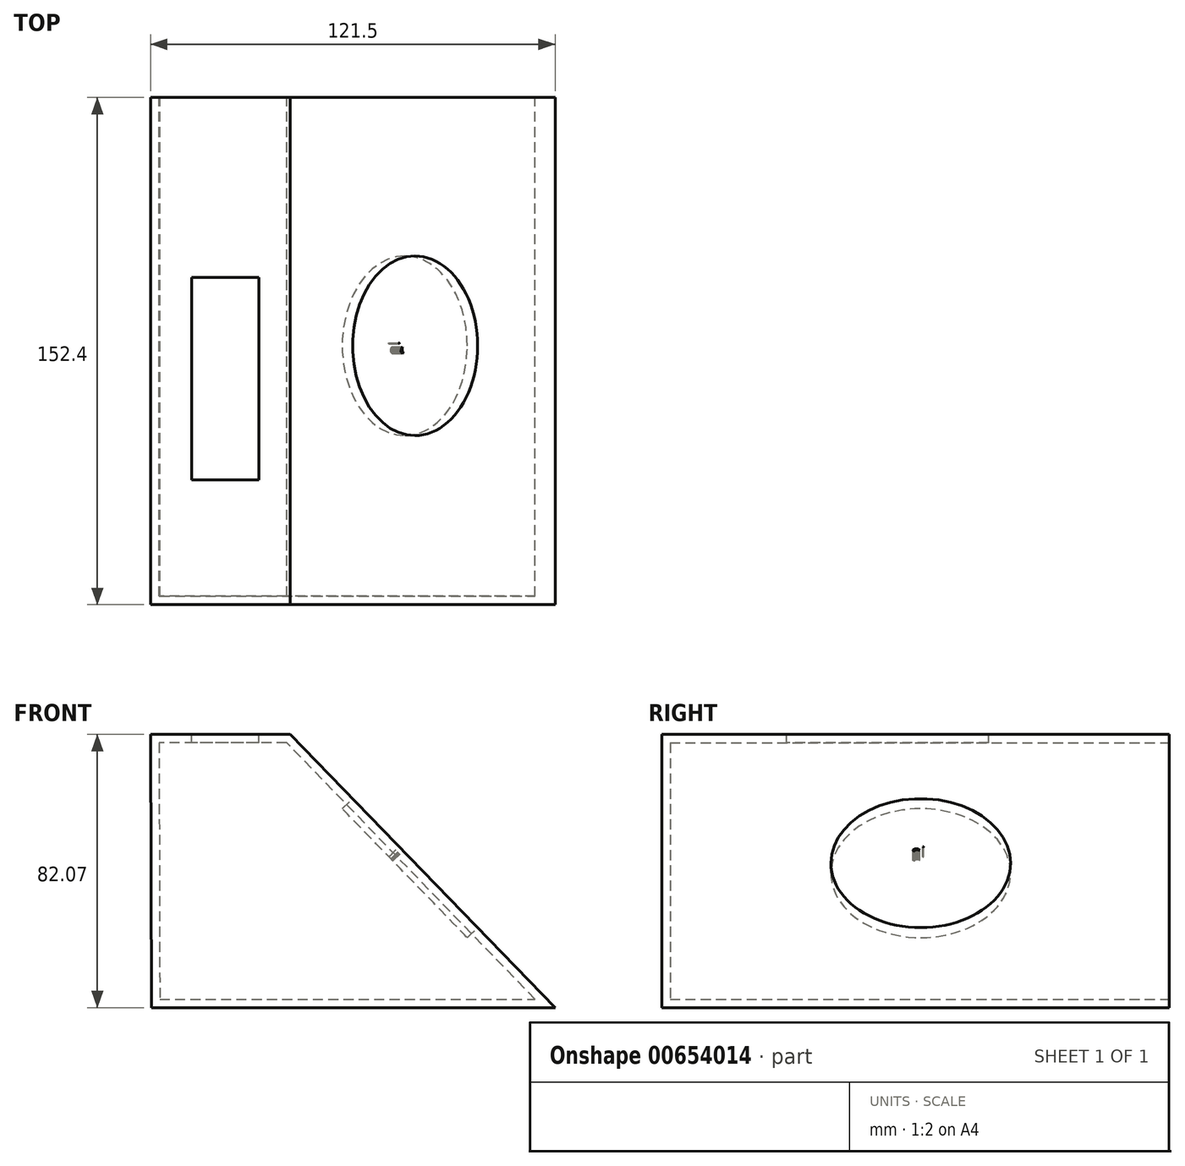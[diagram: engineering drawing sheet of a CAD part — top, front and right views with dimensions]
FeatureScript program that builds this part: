
annotation { "Feature Type Name" : "Feature", "Feature Type Description" : "" }
export const myFeature = defineFeature(function(context is Context, id is Id, definition is map)
    precondition{}
    {
        {
            var Q0;
            Q0=qCreatedBy(makeId("Front.planeOp"),FACE);
            var sketch = newSketch(context, id + "F0", { "sketchPlane" : qUnion([Q0])});
            skLineSegment(sketch, "E0", {"start": v(-59.5, -35.42) * mm, "end": v(61.78, -35.42) * mm});
            skLineSegment(sketch, "E1", {"start": v(61.78, -35.42) * mm, "end": v(-17.77, 46.65) * mm});
            skLineSegment(sketch, "E2", {"start": v(-17.77, 46.65) * mm, "end": v(-59.72, 46.65) * mm});
            skLineSegment(sketch, "E3", {"start": v(-59.72, 46.65) * mm, "end": v(-59.5, -35.42) * mm});
            skSolve(sketch);
        }
        {
            var Q0;
            Q0=makeQuery(id+"F0.imprint","IMPRINT",FACE,{"disambiguationData":[TD([[makeQuery(id+"F0.imprint","IMPRINT",EDGE,{"derivedFrom":sQuery(id+"F0.wireOp",EDGE,"E0")}),1.0]])]});
            extrude(context, id + "F1", {"entities" : qUnion([Q0]), "depth" : 152.4 * mm, "offsetDistance" : 25.4 * mm});
        }
        {
            var Q0;
            Q0=makeQuery(id+"F1.opExtrude","CAP_FACE",FACE,{"disambiguationData":[OSD([sQuery(id+"F0.wireOp",EDGE,"E0"),sQuery(id+"F0.wireOp",EDGE,"E1"),sQuery(id+"F0.wireOp",EDGE,"E2"),sQuery(id+"F0.wireOp",EDGE,"E3")])],"isStart":true});
            var Q1;
            Q1=makeQuery(id+"FHftFUIEuzboTOy_1.boolean.opBoolean","COPY",FACE,{"derivedFrom":makeQuery(id+"FHftFUIEuzboTOy_1.opExtrude","SWEPT_FACE",FACE,{"disambiguationData":[OSD([sQuery(id+"FhygIm2fGgisZin_1.wireOp",EDGE,"3zrmq9q6-JKVG-zBgU-pCQW-6CpuXbiN4dUc.right")])]})});
            shell(context, id + "F2", {"entities" : qUnion([Q0, Q1]), "thickness" : 2.54 * mm});
        }
        {
            var Q0;
            Q0=makeQuery(id+"F1.opExtrude","SWEPT_FACE",FACE,{"disambiguationData":[OSD([sQuery(id+"F0.wireOp",EDGE,"E1")])]});
            var sketch = newSketch(context, id + "F3", { "sketchPlane" : qUnion([Q0])});
            skCircle(sketch, "E4", {"center": v(-74.6, -7.98) * mm, "radius": 26.98 * mm});
            skFitSpline(sketch, "E5", {"points": [v(-77.65, -4.2) * mm, v(-77.2, -4.2) * mm, v(-77.04, -3.74) * mm, v(-77.04, -3.39) * mm, v(-77.22, -3.21) * mm, v(-77.33, -3.02) * mm, v(-77.17, -2.94) * mm, v(-77.3, -2.87) * mm, v(-77.46, -2.87) * mm, v(-77.58, -2.67) * mm, v(-77.53, -2.42) * mm, v(-77.33, -2.4) * mm, v(-77.43, -2.23) * mm, v(-77.4, -2) * mm, v(-77.27, -1.84) * mm, v(-77.27, -1.53) * mm, v(-77.22, -1.3) * mm, v(-77.1, -1.24) * mm, v(-76.92, -1.24) * mm, v(-76.86, -1.15) * mm, v(-76.9, -0.95) * mm, v(-76.72, -0.86) * mm, v(-76.52, -0.86) * mm, v(-76.36, -0.97) * mm, v(-76.28, -1.07) * mm, v(-76.21, -1.26) * mm, v(-76.04, -1.24) * mm, v(-75.8, -1.38) * mm, v(-75.65, -1.53) * mm], "startDerivative": vector(10.08, -2.27) * mm, "endDerivative": vector(3.46, -4.3) * mm});
            skFitSpline(sketch, "E6", {"points": [v(-75.56, -1.51) * mm, v(-75.4, -1.63) * mm, v(-75.17, -1.74) * mm, v(-75.04, -1.9) * mm, v(-74.9, -1.98) * mm, v(-74.75, -2.15) * mm, v(-74.66, -2.34) * mm, v(-74.54, -2.38) * mm, v(-74.49, -2.5) * mm, v(-74.45, -2.17) * mm, v(-74.45, -1.94) * mm, v(-74.45, -1.8) * mm, v(-74.4, -1.96) * mm, v(-74.36, -1.65) * mm, v(-74.34, -1.78) * mm, v(-74.3, -1.44) * mm, v(-74.24, -1.59) * mm, v(-74.17, -1.3) * mm, v(-74.04, -1.2) * mm, v(-74.06, -1.36) * mm, v(-73.96, -1.07) * mm, v(-73.96, -1.2) * mm], "startDerivative": vector(3.2, -2.61) * mm, "endDerivative": vector(-0.57, -6) * mm});
            skFitSpline(sketch, "E7", {"points": [v(-77.65, -4.2) * mm, v(-77.65, -4.43) * mm, v(-77.48, -4.49) * mm, v(-77.33, -4.53) * mm, v(-77.2, -4.49) * mm, v(-77.07, -4.5) * mm, v(-76.9, -4.43) * mm, v(-76.77, -4.41) * mm, v(-76.72, -4.24) * mm, v(-76.63, -4.24) * mm, v(-76.61, -3.97) * mm, v(-76.54, -3.9) * mm, v(-76.46, -4.24) * mm, v(-76.32, -4.24) * mm, v(-76.24, -4.4) * mm, v(-76.06, -4.24) * mm, v(-75.9, -4.24) * mm, v(-75.72, -4.4) * mm, v(-75.53, -4.43) * mm, v(-75.47, -4.76) * mm, v(-75.32, -4.86) * mm, v(-75.2, -5.01) * mm, v(-75.25, -5.1) * mm, v(-75.24, -5.5) * mm, v(-75.06, -5.53) * mm, v(-75.02, -5.67) * mm, v(-74.9, -5.79) * mm, v(-74.92, -6) * mm, v(-75.11, -6.04) * mm, v(-75.25, -6.08) * mm, v(-75.3, -6.2) * mm, v(-75.21, -6.4) * mm, v(-75.03, -6.44) * mm, v(-74.88, -6.44) * mm, v(-74.74, -6.4) * mm, v(-74.54, -6.29) * mm, v(-74.42, -6.11) * mm, v(-74.3, -6.04) * mm, v(-74.18, -5.82) * mm, v(-74.07, -5.6) * mm, v(-73.95, -5.2) * mm, v(-73.95, -5.05) * mm, v(-73.95, -4.86) * mm, v(-73.95, -4.59) * mm, v(-73.95, -4.2) * mm, v(-73.95, -3.99) * mm, v(-73.95, -3.8) * mm, v(-73.95, -3.64) * mm, v(-73.71, -3.5) * mm, v(-73.54, -3.39) * mm, v(-73.35, -3.33) * mm, v(-73.18, -3.25) * mm, v(-73.06, -3.21) * mm, v(-73.02, -3.08) * mm, v(-73.03, -2.94) * mm, v(-73.13, -2.87) * mm, v(-73.27, -2.73) * mm, v(-73.43, -2.71) * mm, v(-73.67, -2.73) * mm, v(-73.8, -2.85) * mm, v(-73.95, -2.92) * mm, v(-73.95, -2.73) * mm, v(-73.95, -2.52) * mm, v(-73.95, -2.29) * mm, v(-73.95, -2.05) * mm, v(-73.78, -1.92) * mm, v(-73.64, -1.8) * mm, v(-73.43, -1.65) * mm, v(-73.25, -1.65) * mm, v(-73.18, -1.51) * mm, v(-73.18, -1.13) * mm, v(-73.14, -1.13) * mm, v(-73.09, -0.9) * mm, v(-73.14, -0.76) * mm, v(-73.18, -0.41) * mm, v(-73.23, -0.22) * mm, v(-73.4, -0.2) * mm, v(-73.52, -0.26) * mm, v(-73.57, -0.58) * mm, v(-73.6, -0.95) * mm, v(-73.66, -1.13) * mm, v(-73.77, -1.13) * mm], "startDerivative": vector(-4.15, -20.85) * mm, "endDerivative": vector(-13.48, 3.08) * mm});
            skFitSpline(sketch, "E8", {"points": [v(-73.73, -1.13) * mm, v(-73.77, -1.13) * mm, v(-73.95, -1.13) * mm, v(-73.73, -1.13) * mm]});
            skLineSegment(sketch, "E9", {"start": v(-76.91, -2.54) * mm, "end": v(-76.74, -2.38) * mm});
            skLineSegment(sketch, "E10", {"start": v(-76.74, -2.38) * mm, "end": v(-76.63, -2.1) * mm});
            skLineSegment(sketch, "E11", {"start": v(-76.63, -2.1) * mm, "end": v(-76.5, -2.1) * mm});
            skLineSegment(sketch, "E12", {"start": v(-76.5, -2.1) * mm, "end": v(-76.4, -1.98) * mm});
            skLineSegment(sketch, "E13", {"start": v(-76.4, -1.98) * mm, "end": v(-76.24, -1.98) * mm});
            skLineSegment(sketch, "E14", {"start": v(-76.24, -1.98) * mm, "end": v(-76.03, -1.98) * mm});
            skLineSegment(sketch, "E15", {"start": v(-76.03, -1.98) * mm, "end": v(-75.85, -2) * mm});
            skLineSegment(sketch, "E16", {"start": v(-75.85, -2) * mm, "end": v(-75.7, -1.98) * mm});
            skLineSegment(sketch, "E17", {"start": v(-75.7, -1.98) * mm, "end": v(-75.58, -2) * mm});
            skLineSegment(sketch, "E18", {"start": v(-75.58, -2) * mm, "end": v(-75.4, -2.08) * mm});
            skLineSegment(sketch, "E19", {"start": v(-75.4, -2.08) * mm, "end": v(-75.33, -2.19) * mm});
            skLineSegment(sketch, "E20", {"start": v(-75.33, -2.19) * mm, "end": v(-75.11, -2.23) * mm});
            skLineSegment(sketch, "E21", {"start": v(-75.11, -2.23) * mm, "end": v(-75.02, -2.41) * mm});
            skLineSegment(sketch, "E22", {"start": v(-75.02, -2.41) * mm, "end": v(-74.83, -2.58) * mm});
            skLineSegment(sketch, "E23", {"start": v(-75.18, -2.47) * mm, "end": v(-75.29, -2.47) * mm});
            skLineSegment(sketch, "E24", {"start": v(-75.29, -2.47) * mm, "end": v(-75.48, -2.4) * mm});
            skLineSegment(sketch, "E25", {"start": v(-75.48, -2.4) * mm, "end": v(-75.64, -2.4) * mm});
            skLineSegment(sketch, "E26", {"start": v(-75.64, -2.4) * mm, "end": v(-75.77, -2.38) * mm});
            skLineSegment(sketch, "E27", {"start": v(-75.77, -2.38) * mm, "end": v(-76.08, -2.36) * mm});
            skLineSegment(sketch, "E28", {"start": v(-76.08, -2.36) * mm, "end": v(-76.15, -2.47) * mm});
            skLineSegment(sketch, "E29", {"start": v(-76.15, -2.47) * mm, "end": v(-76.3, -2.58) * mm});
            skLineSegment(sketch, "E30", {"start": v(-76.3, -2.58) * mm, "end": v(-76.41, -2.82) * mm});
            skLineSegment(sketch, "E31", {"start": v(-76.7, -2.8) * mm, "end": v(-76.83, -2.82) * mm});
            skLineSegment(sketch, "E32", {"start": v(-76.83, -2.82) * mm, "end": v(-76.94, -2.7) * mm});
            skLineSegment(sketch, "E33", {"start": v(-76.94, -2.7) * mm, "end": v(-76.91, -2.54) * mm});
            skLineSegment(sketch, "E34", {"start": v(-76.7, -2.8) * mm, "end": v(-76.41, -2.82) * mm});
            skLineSegment(sketch, "E35", {"start": v(-75.18, -2.47) * mm, "end": v(-74.83, -2.58) * mm});
            skLineSegment(sketch, "E36", {"start": v(-75.92, -2.82) * mm, "end": v(-76.1, -2.82) * mm});
            skLineSegment(sketch, "E37", {"start": v(-76.1, -2.68) * mm, "end": v(-76, -2.58) * mm});
            skLineSegment(sketch, "E38", {"start": v(-76, -2.58) * mm, "end": v(-75.88, -2.64) * mm});
            skLineSegment(sketch, "E39", {"start": v(-75.88, -2.64) * mm, "end": v(-75.64, -2.54) * mm});
            skLineSegment(sketch, "E40", {"start": v(-75.64, -2.54) * mm, "end": v(-75.6, -2.64) * mm});
            skLineSegment(sketch, "E41", {"start": v(-75.6, -2.64) * mm, "end": v(-75.46, -2.68) * mm});
            skLineSegment(sketch, "E42", {"start": v(-75.46, -2.68) * mm, "end": v(-75.25, -2.68) * mm});
            skLineSegment(sketch, "E43", {"start": v(-75.25, -2.68) * mm, "end": v(-75.18, -2.75) * mm});
            skLineSegment(sketch, "E44", {"start": v(-75.18, -2.75) * mm, "end": v(-75.03, -2.84) * mm});
            skLineSegment(sketch, "E45", {"start": v(-75.03, -2.84) * mm, "end": v(-74.94, -2.92) * mm});
            skLineSegment(sketch, "E46", {"start": v(-74.94, -2.92) * mm, "end": v(-74.95, -3.01) * mm});
            skLineSegment(sketch, "E47", {"start": v(-74.95, -3.01) * mm, "end": v(-75.06, -3.09) * mm});
            skLineSegment(sketch, "E48", {"start": v(-75.02, -3.24) * mm, "end": v(-74.83, -3.24) * mm});
            skLineSegment(sketch, "E49", {"start": v(-74.83, -3.24) * mm, "end": v(-74.66, -3.5) * mm});
            skLineSegment(sketch, "E50", {"start": v(-74.66, -3.5) * mm, "end": v(-74.54, -3.55) * mm});
            skLineSegment(sketch, "E51", {"start": v(-74.54, -3.55) * mm, "end": v(-74.44, -3.6) * mm});
            skLineSegment(sketch, "E52", {"start": v(-74.44, -3.6) * mm, "end": v(-74.44, -3.81) * mm});
            skLineSegment(sketch, "E53", {"start": v(-74.44, -3.81) * mm, "end": v(-74.42, -4.04) * mm});
            skLineSegment(sketch, "E54", {"start": v(-74.42, -4.04) * mm, "end": v(-74.42, -4.34) * mm});
            skLineSegment(sketch, "E55", {"start": v(-74.42, -4.34) * mm, "end": v(-74.42, -4.56) * mm});
            skLineSegment(sketch, "E56", {"start": v(-74.42, -4.56) * mm, "end": v(-74.47, -4.8) * mm});
            skLineSegment(sketch, "E57", {"start": v(-74.47, -4.8) * mm, "end": v(-74.6, -4.62) * mm});
            skLineSegment(sketch, "E58", {"start": v(-74.6, -4.62) * mm, "end": v(-74.82, -4.41) * mm});
            skLineSegment(sketch, "E59", {"start": v(-74.82, -4.41) * mm, "end": v(-74.97, -4.28) * mm});
            skLineSegment(sketch, "E60", {"start": v(-74.97, -4.28) * mm, "end": v(-75.03, -4.23) * mm});
            skLineSegment(sketch, "E61", {"start": v(-75.03, -4.23) * mm, "end": v(-75.25, -4.2) * mm});
            skLineSegment(sketch, "E62", {"start": v(-75.25, -4.2) * mm, "end": v(-75.33, -4.17) * mm});
            skLineSegment(sketch, "E63", {"start": v(-75.33, -4.17) * mm, "end": v(-75.37, -4.06) * mm});
            skLineSegment(sketch, "E64", {"start": v(-75.37, -4.06) * mm, "end": v(-75.26, -4.02) * mm});
            skLineSegment(sketch, "E65", {"start": v(-75.26, -4.02) * mm, "end": v(-75.26, -3.83) * mm});
            skLineSegment(sketch, "E66", {"start": v(-75.26, -3.83) * mm, "end": v(-75.44, -3.8) * mm});
            skLineSegment(sketch, "E67", {"start": v(-75.44, -3.8) * mm, "end": v(-75.56, -3.8) * mm});
            skLineSegment(sketch, "E68", {"start": v(-75.56, -3.8) * mm, "end": v(-75.68, -3.85) * mm});
            skLineSegment(sketch, "E69", {"start": v(-75.68, -3.85) * mm, "end": v(-75.73, -4.04) * mm});
            skLineSegment(sketch, "E70", {"start": v(-75.73, -4.04) * mm, "end": v(-75.92, -4.08) * mm});
            skLineSegment(sketch, "E71", {"start": v(-75.92, -4.08) * mm, "end": v(-76.1, -4) * mm});
            skLineSegment(sketch, "E72", {"start": v(-76.1, -4) * mm, "end": v(-76.2, -3.9) * mm});
            skLineSegment(sketch, "E73", {"start": v(-76.2, -3.9) * mm, "end": v(-76.33, -3.83) * mm});
            skLineSegment(sketch, "E74", {"start": v(-76.33, -3.83) * mm, "end": v(-76.3, -3.6) * mm});
            skLineSegment(sketch, "E75", {"start": v(-76.3, -3.6) * mm, "end": v(-76.28, -3.44) * mm});
            skLineSegment(sketch, "E76", {"start": v(-76.28, -3.44) * mm, "end": v(-76.1, -3.25) * mm});
            skLineSegment(sketch, "E77", {"start": v(-76.1, -3.25) * mm, "end": v(-75.93, -3.25) * mm});
            skLineSegment(sketch, "E78", {"start": v(-75.93, -3.25) * mm, "end": v(-75.85, -3.16) * mm});
            skLineSegment(sketch, "E79", {"start": v(-75.85, -3.16) * mm, "end": v(-75.81, -3) * mm});
            skLineSegment(sketch, "E80", {"start": v(-75.81, -3) * mm, "end": v(-75.78, -2.9) * mm});
            skLineSegment(sketch, "E81", {"start": v(-75.78, -2.9) * mm, "end": v(-75.92, -2.79) * mm});
            skSolve(sketch);
        }
        {
            var Q0;
            Q0=makeQuery(id+"F1.opExtrude","SWEPT_FACE",FACE,{"disambiguationData":[OSD([sQuery(id+"F0.wireOp",EDGE,"E2")])]});
            var sketch = newSketch(context, id + "F4", { "sketchPlane" : qUnion([Q0])});
            skLineSegment(sketch, "E82.bottom", {"start": v(-47.44, -114.85) * mm, "end": v(-27.2, -114.85) * mm});
            skLineSegment(sketch, "E82.top", {"start": v(-47.44, -54.13) * mm, "end": v(-27.2, -54.13) * mm});
            skLineSegment(sketch, "E82.left", {"start": v(-47.44, -114.85) * mm, "end": v(-47.44, -54.13) * mm});
            skLineSegment(sketch, "E82.right", {"start": v(-27.2, -114.85) * mm, "end": v(-27.2, -54.13) * mm});
            skSolve(sketch);
        }
        {
            var Q0;
            Q0=makeQuery(id+"F3.imprint","IMPRINT",FACE,{"disambiguationData":[TD([[makeQuery(id+"F3.imprint","IMPRINT",EDGE,{"derivedFrom":sQuery(id+"F3.wireOp",EDGE,"E4")}),1.0]])]});
            extrude(context, id + "F5", {"entities" : qUnion([Q0]), "oppositeDirection" : true, "depth" : 4.32 * mm, "offsetDistance" : 25.4 * mm});
        }
        {
            var Q0;
            Q0=makeQuery(id+"F4.imprint","IMPRINT",FACE,{"disambiguationData":[TD([[makeQuery(id+"F4.imprint","IMPRINT",EDGE,{"derivedFrom":sQuery(id+"F4.wireOp",EDGE,"E82.bottom")}),1.0]])]});
            extrude(context, id + "F6", {"entities" : qUnion([Q0]), "operationType" : NewBodyOperationType.REMOVE, "oppositeDirection" : true, "depth" : 25.4 * mm, "offsetDistance" : 25.4 * mm});
        }
    });
